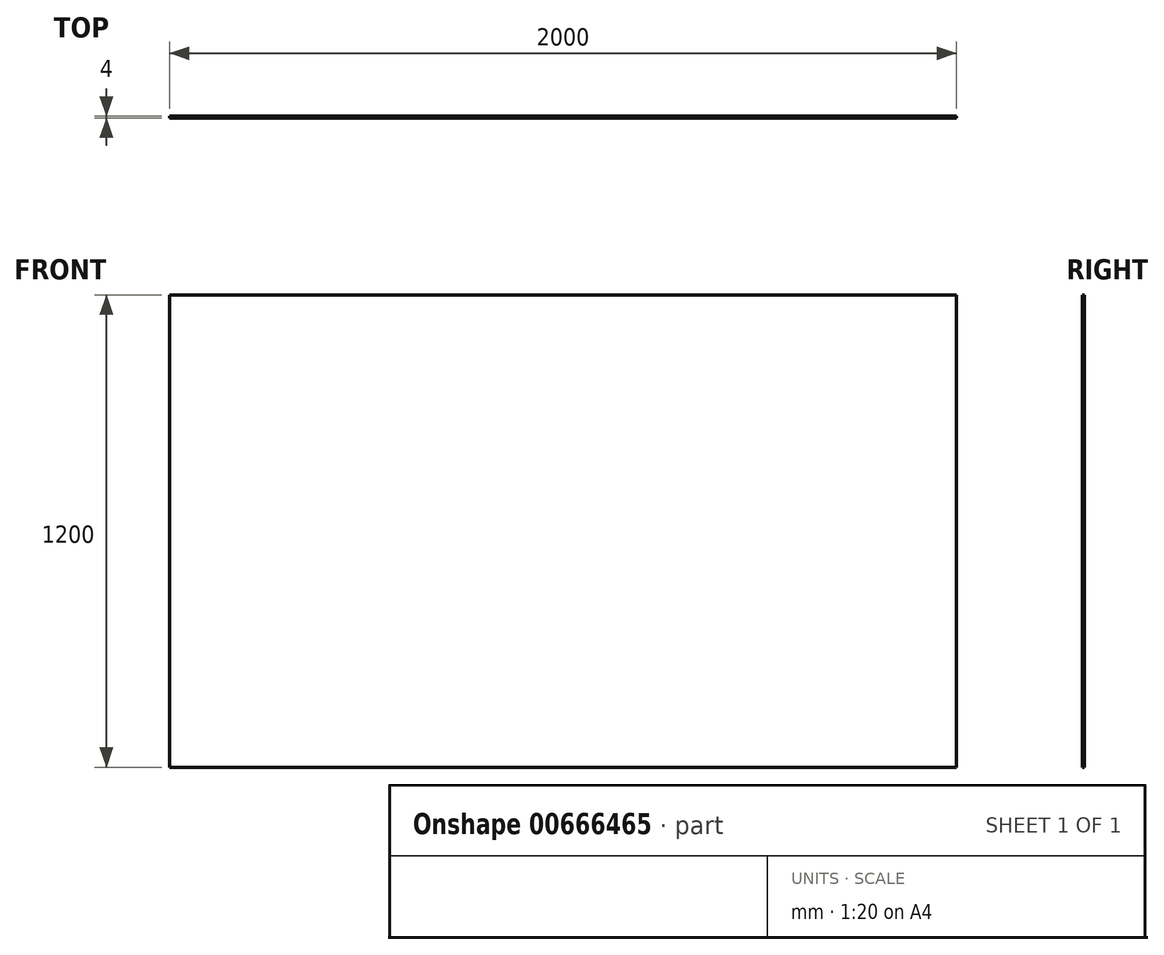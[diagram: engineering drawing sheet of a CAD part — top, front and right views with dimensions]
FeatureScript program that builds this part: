
annotation { "Feature Type Name" : "Feature", "Feature Type Description" : "" }
export const myFeature = defineFeature(function(context is Context, id is Id, definition is map)
    precondition{}
    {
        {
            var Q0;
            Q0=qCreatedBy(makeId("Front.planeOp"),FACE);
            var sketch = newSketch(context, id + "F0", { "sketchPlane" : qUnion([Q0])});
            skLineSegment(sketch, "E0.bottom", {"start": v(-989.79, 638.19) * mm, "end": v(1010.21, 638.19) * mm});
            skLineSegment(sketch, "E0.top", {"start": v(-989.79, -561.81) * mm, "end": v(1010.21, -561.81) * mm});
            skLineSegment(sketch, "E0.left", {"start": v(-989.79, 638.19) * mm, "end": v(-989.79, -561.81) * mm});
            skLineSegment(sketch, "E0.right", {"start": v(1010.21, 638.19) * mm, "end": v(1010.21, -561.81) * mm});
            skSolve(sketch);
        }
        {
            var Q0;
            Q0 = qSketchRegion(id + "F0", true);
            extrude(context, id + "F1", {"entities" : qUnion([Q0]), "depth" : 4 * mm, "offsetDistance" : 25 * mm});
        }
    });
